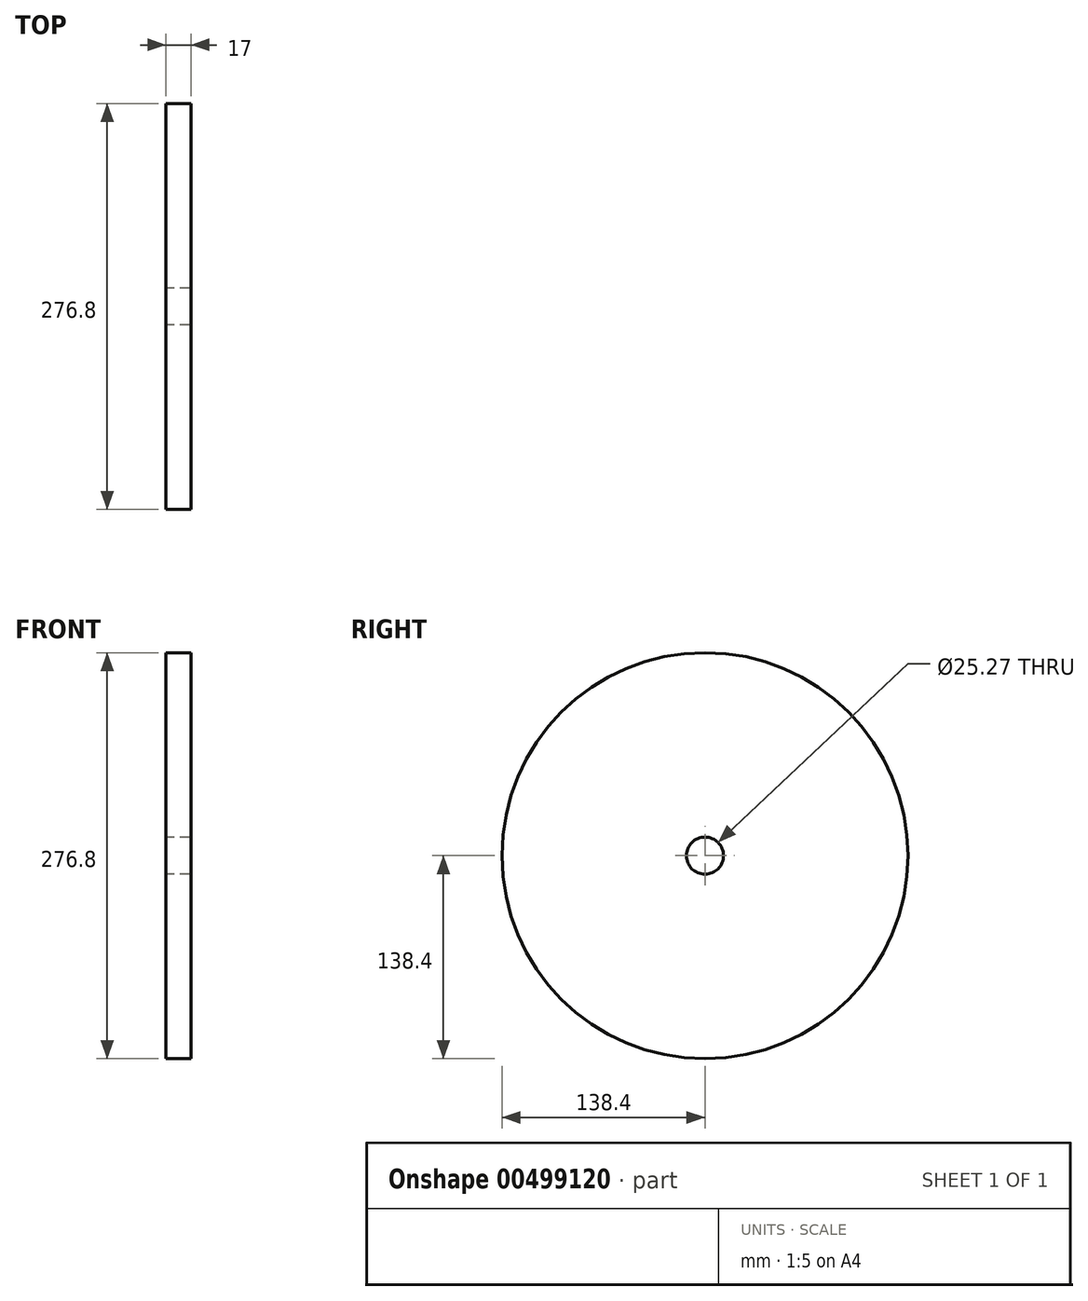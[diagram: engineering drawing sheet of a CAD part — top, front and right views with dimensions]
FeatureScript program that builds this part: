
annotation { "Feature Type Name" : "Feature", "Feature Type Description" : "" }
export const myFeature = defineFeature(function(context is Context, id is Id, definition is map)
    precondition{}
    {
        {
            var Q0;
            Q0=qCreatedBy(makeId("Right.planeOp"),FACE);
            var sketch = newSketch(context, id + "F0", { "sketchPlane" : qUnion([Q0])});
            skCircle(sketch, "E0", {"center": v(0, 0) * mm, "radius": 138.4 * mm});
            skCircle(sketch, "E1", {"center": v(0, 0) * mm, "radius": 12.63 * mm});
            skSolve(sketch);
        }
        {
            var Q0;
            Q0 = qSketchRegion(id + "F0", true);
            extrude(context, id + "F1", {"entities" : qUnion([Q0]), "depth" : 17 * mm, "offsetDistance" : 25 * mm});
        }
    });
